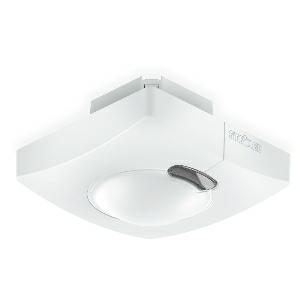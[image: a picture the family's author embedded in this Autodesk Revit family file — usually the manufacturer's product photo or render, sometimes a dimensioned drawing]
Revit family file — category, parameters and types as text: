
# Revit family: hf_3360_033675
name_source: partatom
category: Elektroinstallationen
revit_build: Autodesk Revit 2016 (Build: 20190508_0715(x64)
units: mm (PartAtom-declared; Revit-internal decimal feet)

## family parameters
Basisbauteil = Fläche
Beim Laden mit Abzugskörper schneiden = Nein
Bemaßung runder Anschluss = Durchmesser verwenden
Beschriftungsausrichtung beibehalten = Nein
Gemeinsam genutzt = Nein
Raumberechnungspunkt = Nein
Teiletyp = Normal

## types (1)
- HF 3360
    Apparent Load = 0 VA
    Beschreibung = Type: Motion detectors; Dimensions (L x W x H): 64 x 94 x 94 mm; Mains power supply: 220 – 240 V / 50 – 60 Hz; Sensor Technology: High frequency; Application, place: Indoors; Application, room: function room / ancillary room, stairwell, WC / washroom, multi-storey / underground car park, Indoors; Installation site: wall, ceiling, corner; Installation: Concealed wiring; HF-system: 5,8 GHz; Electronic scalability: Yes; Mechanical scalability: No; Mounting height: 2,00 – 4,00 m; Optimum mounting height: 2,8 m; Detection: also through glass, wood and stud walls; Detection angle: 360 °; Angle of aperture: 140 °; Sneak-by guard: Yes; Reach, radial: Ø 8 m (50 m²); Reach, tangential: Ø 8 m (50 m²); Twilight setting TEACH: Yes; Twilight setting: 2 – 1000 lx; Time setting: 5 sec – 15 min; Switching output 1, resistive: 2000 W; Switching output 1, number of LEDs / fluorescent lamps: 8 pcs.; Constant-lighting control: No; Basic light level function: No; Functions: Normal / test mode, Manual ON / ON-OFF; Settings via: Remote control, Potentiometers, Smart Remote; With remote control: No; Interconnection: Yes; IP-rating: IP20; Material: Plastic; Ambient temperature: -20 – 50 °C; Colour: white; Colour, RAL: 9003; Manufacturer's Warranty: 5 years; Version: COM1 - concealed, sq.; PU1, EAN: 4007841033675
    Height = 94 mm  [stored 0.308399 ft]
    Hersteller = Steinel
    Length = 64 mm
    ModVariant = Nein
    Modell = 033675
    Mounting Type = Recessed
    Number of Poles = 1
    OnlyDefault = Ja
    Power Factor = 1
    Product Name = HF 3360
    Product group = Sensor-switched indoor light
    ProductGroupID = 30
    Protection Class = Protection class
    Protection Degree = IP 20
    RlxData = <blob elided: 27001 chars, md5=a2f88e98>
    SensorDataFile = {"IESDataFiles":[]}
    Typenbild = produkt1_033675.jpg
    Typenkommentare = Product without accessories
    URL = http://relux.com
    VarID = ---
    Voltage = 0 V
    Vorgabe-Ansicht = 1800 mm
    Weight = 0.00 kg
    Width = 94 mm  [stored 0.308399 ft]

note: [stored X ft] marks values corroborated as IEEE doubles in the binary element streams (Revit-internal decimal feet)

## geometry (parser evidence)
native form markers: Blend x4, Sweep x9
no freeform markers — native parametric forms only
